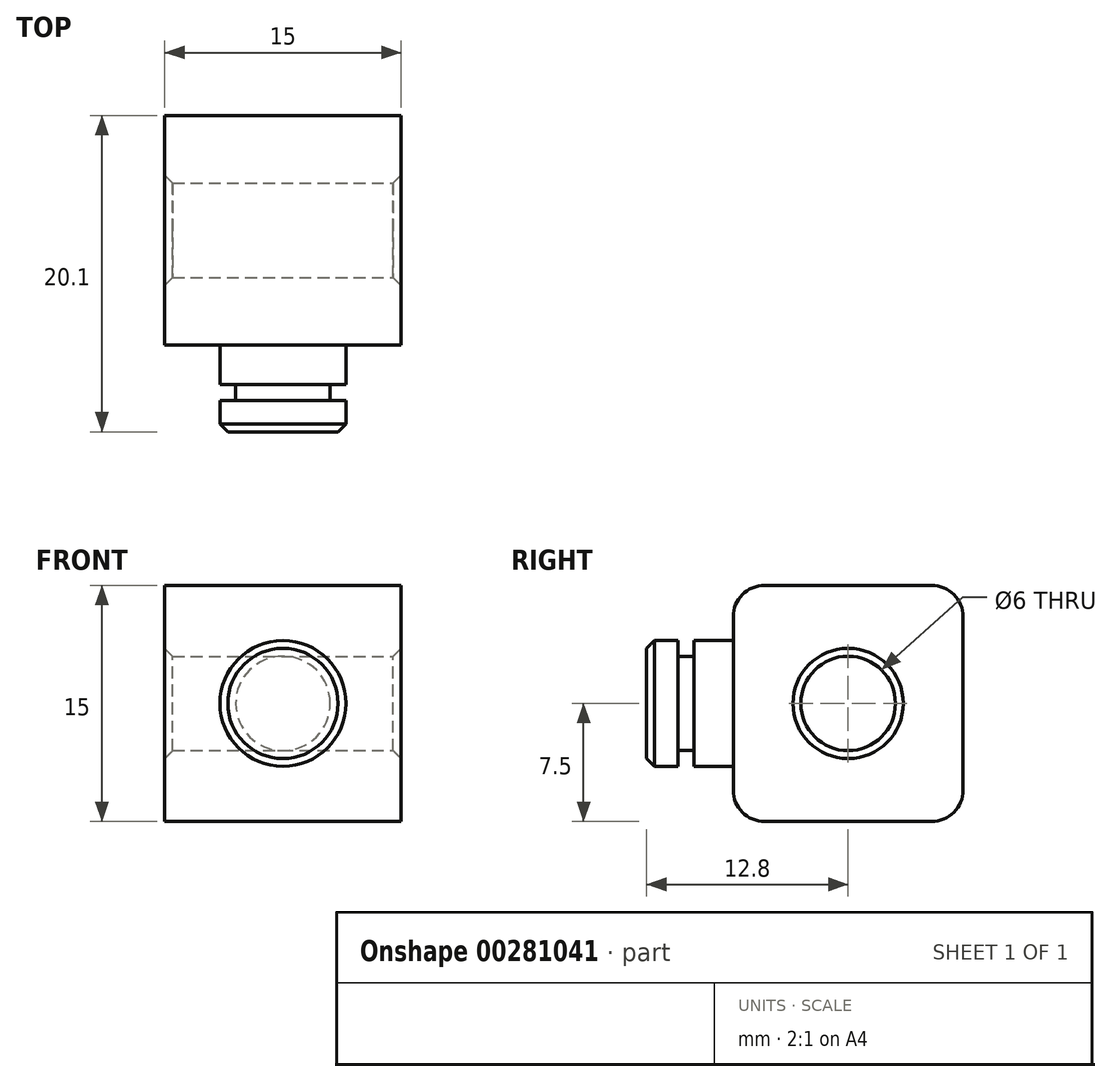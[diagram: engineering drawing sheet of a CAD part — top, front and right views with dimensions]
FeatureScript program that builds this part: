
annotation { "Feature Type Name" : "Feature", "Feature Type Description" : "" }
export const myFeature = defineFeature(function(context is Context, id is Id, definition is map)
    precondition{}
    {
        {
            var Q0;
            Q0=qCreatedBy(makeId("Right.planeOp"),FACE);
            var sketch = newSketch(context, id + "F0", { "sketchPlane" : qUnion([Q0])});
            skLineSegment(sketch, "E0.bottom", {"start": v(7.3, -7.5) * mm, "end": v(-7.3, -7.5) * mm});
            skLineSegment(sketch, "E0.top", {"start": v(7.3, 7.5) * mm, "end": v(-7.3, 7.5) * mm});
            skLineSegment(sketch, "E0.left", {"start": v(7.3, -7.5) * mm, "end": v(7.3, 7.5) * mm});
            skLineSegment(sketch, "E0.right", {"start": v(-7.3, -7.5) * mm, "end": v(-7.3, 7.5) * mm});
            skPoint(sketch, "E0.middle", {"position": v(0, 0) * mm});
            skSolve(sketch);
        }
        {
            var Q0;
            Q0 = qSketchRegion(id + "F0", true);
            extrude(context, id + "F1", {"entities" : qUnion([Q0]), "oppositeDirection" : true, "depth" : 15 * mm});
        }
        {
            var Q0;
            Q0=makeQuery(id+"F1.opExtrude","SWEPT_EDGE",EDGE,{"disambiguationData":[OSD([sQuery(id+"F0.wireOp",EDGE,"E0.top"),sQuery(id+"F0.wireOp",EDGE,"E0.right")])]});
            var Q1;
            Q1=makeQuery(id+"F1.opExtrude","SWEPT_EDGE",EDGE,{"disambiguationData":[OSD([sQuery(id+"F0.wireOp",EDGE,"E0.top"),sQuery(id+"F0.wireOp",EDGE,"E0.left")])]});
            var Q2;
            Q2=makeQuery(id+"F1.opExtrude","SWEPT_EDGE",EDGE,{"disambiguationData":[OSD([sQuery(id+"F0.wireOp",EDGE,"E0.bottom"),sQuery(id+"F0.wireOp",EDGE,"E0.right")])]});
            var Q3;
            Q3=makeQuery(id+"F1.opExtrude","SWEPT_EDGE",EDGE,{"disambiguationData":[OSD([sQuery(id+"F0.wireOp",EDGE,"E0.bottom"),sQuery(id+"F0.wireOp",EDGE,"E0.left")])]});
            fillet(context, id + "F2", {"entities" : qUnion([Q0, Q1, Q2, Q3]), "radius" : 2 * mm, "tangentPropagation" : true, "allowEdgeOverflow" : false});
        }
        {
            var Q0;
            Q0=makeQuery(id+"F1.opExtrude","CAP_FACE",FACE,{"disambiguationData":[OSD([sQuery(id+"F0.wireOp",EDGE,"E0.bottom"),sQuery(id+"F0.wireOp",EDGE,"E0.top"),sQuery(id+"F0.wireOp",EDGE,"E0.left"),sQuery(id+"F0.wireOp",EDGE,"E0.right")])],"isStart":true});
            var sketch = newSketch(context, id + "F3", { "sketchPlane" : qUnion([Q0])});
            skCircle(sketch, "E1", {"center": v(0, 0) * mm, "radius": 3 * mm});
            skSolve(sketch);
        }
        {
            var Q0;
            Q0 = qSketchRegion(id + "F3", true);
            extrude(context, id + "F4", {"entities" : qUnion([Q0]), "operationType" : NewBodyOperationType.REMOVE, "endBound" : BoundingType.THROUGH_ALL, "oppositeDirection" : true, "depth" : 25 * mm});
        }
        {
            var Q0;
            Q0=makeQuery(id+"F4.boolean.opBoolean","COPY",FACE,{"derivedFrom":makeQuery(id+"F4.opExtrude","SWEPT_FACE",FACE,{"disambiguationData":[OSD([sQuery(id+"F3.wireOp",EDGE,"E1")])]})});
            chamfer(context, id + "F5", {"entities" : qUnion([Q0]), "chamferType" : ChamferType.OFFSET_ANGLE, "width" : .5 * mm, "oppositeDirection" : false, "angle" : 45 * degree, "tangentPropagation" : true});
        }
        {
            var Q0;
            Q0=makeQuery(id+"F1.opExtrude","CAP_FACE",FACE,{"disambiguationData":[OSD([sQuery(id+"F0.wireOp",EDGE,"E0.bottom"),sQuery(id+"F0.wireOp",EDGE,"E0.top"),sQuery(id+"F0.wireOp",EDGE,"E0.left"),sQuery(id+"F0.wireOp",EDGE,"E0.right")])],"isStart":true});
            var Q1;
            Q1=makeQuery(id+"F1.opExtrude","CAP_FACE",FACE,{"disambiguationData":[OSD([sQuery(id+"F0.wireOp",EDGE,"E0.bottom"),sQuery(id+"F0.wireOp",EDGE,"E0.top"),sQuery(id+"F0.wireOp",EDGE,"E0.left"),sQuery(id+"F0.wireOp",EDGE,"E0.right")])],"isStart":false});
            cPlane(context, id + "F6", {"entities" : qUnion([Q0, Q1]), "cplaneType" : CPlaneType.MID_PLANE, "offset" : 25 * mm, "width" : 150 * mm, "height" : 150 * mm});
        }
        {
            var Q0;
            Q0=qCreatedBy(id+"F6.planeOp",FACE);
            var sketch = newSketch(context, id + "F7", { "sketchPlane" : qUnion([Q0])});
            skLineSegment(sketch, "E2", {"start": v(0, 0) * mm, "end": v(-7.3, 0) * mm, "construction": true});
            skLineSegment(sketch, "E3.0", {"start": v(-7.3, -5.5) * mm, "end": v(-7.3, 5.5) * mm, "construction": true});
            skLineSegment(sketch, "E4", {"start": v(-12.8, 0) * mm, "end": v(-12.8, -4) * mm});
            skLineSegment(sketch, "E5", {"start": v(-12.8, -4) * mm, "end": v(-10.8, -4) * mm});
            skLineSegment(sketch, "E6", {"start": v(-10.8, -4) * mm, "end": v(-10.8, -3) * mm});
            skLineSegment(sketch, "E7", {"start": v(-10.8, -3) * mm, "end": v(-9.8, -3) * mm});
            skLineSegment(sketch, "E8", {"start": v(-9.8, -3) * mm, "end": v(-9.8, -4) * mm});
            skLineSegment(sketch, "E9", {"start": v(-9.8, -4) * mm, "end": v(-7.3, -4) * mm});
            skLineSegment(sketch, "E10", {"start": v(-7.3, -4) * mm, "end": v(-7.3, 0) * mm});
            skLineSegment(sketch, "E11", {"start": v(-7.3, 0) * mm, "end": v(-12.8, 0) * mm});
            skSolve(sketch);
        }
        {
            var Q0;
            Q0=makeQuery(id+"F7.imprint","IMPRINT",FACE,{"disambiguationData":[TD([[makeQuery(id+"F7.imprint","IMPRINT",EDGE,{"derivedFrom":sQuery(id+"F7.wireOp",EDGE,"E4")}),1.0]])]});
            var Q1;
            Q1=sQuery(id+"F7.wireOp",EDGE,"E2");
            revolve(context, id + "F8", {"operationType" : NewBodyOperationType.ADD, "entities" : qUnion([Q0]), "axis" : qUnion([Q1]), "revolveType" : RevolveType.FULL});
        }
        {
            var Q0;
            Q0=makeQuery(id+"F8.opRevolve","SWEPT_EDGE",EDGE,{"disambiguationData":[OSD([sQuery(id+"F7.wireOp",EDGE,"E4"),sQuery(id+"F7.wireOp",EDGE,"E5")])]});
            chamfer(context, id + "F9", {"entities" : qUnion([Q0]), "chamferType" : ChamferType.OFFSET_ANGLE, "width" : .5 * mm, "oppositeDirection" : false, "angle" : 45 * degree, "tangentPropagation" : true});
        }
    });
